# Revit family: 8_天吊埋込タイプ 厨房用 単相100V_3相200V-60
name_source: partatom
category: 機械設備
units: mm (PartAtom-declared; Revit-internal decimal feet)

## family parameters
OmniClass タイトル = Axial Fans
OmniClass 番号 = 23.75.35.17.24
パーツ タイプ = 割り込み
ロード時にボイドで切り取り = いいえ
丸型コネクタ寸法 = 直径を使用
作業面ベース = いいえ
共有 = いいえ
常に垂直 = はい
部屋計算ポイント = はい

## types (6) — shared parameters
Clearance Left = 600
IfcExportAs = IfcFanType
IfcExportType = CENTRIFUGALFORWARDCURVED
M = 85  [stored 0.278871 ft]
MID静圧 = 0.0 Pa
MID風量 = 0.0 m³/h
MIN静圧 = 0.0 Pa
MIN風量 = 0.0 m³/h
OmniClassCode = 23-33 31 19 13 15
URL = https://www.mitsubishielectric.co.jp
Uniclass2015Code = Pr_65_67_29_12
Uniclass2015Title = Centrifugal fans
Uniclass2015Version = Systems v1.9
サービススペース = はい
ドレン管径 = 18 mm
ファンの種類 = 多翼形
仕様書バージョン = Version1.0
企業コード = 108420
分類コード = 50052502100020
周波数 = 60 Hz
呼称 = 消音ボックス付送風機
極 = 4
法定耐用年数 = 15
盤工事区分 = 電気工事
積算_科目 = 2 換気設備
製品リリース年月 = 2019年6月20日
製品出荷対象 = 国内
製造元 = 三菱電機株式会社
設置方法 = 天吊
説明 = ストレートシロッコファン厨房用
負荷分類 = 3_ファン類
運転質量 = 0.00 kg
zero-valued in all types: Clearance Back, Clearance Bottom, Clearance Front, Clearance Right, Clearance Top

## per-type parameters (varying)
| type | Depth | Height | MAX静圧 | MAX風量 | Width | ダクト径 | 価格 | 天吊金具ピッチ奥行 | 天吊金具ピッチ幅 | 形名 | 本体マテリアル | 極数 | 消費電力 | 番手 | 相 | 製品質量 | 質量 | 電動機出力 | 電圧 | 騒音レベル(dB(A)) | 騒音レベル(dB(A))_側面 | 騒音レベル(dB(A))_吐出 | 騒音レベル(dB(A))_吸込 |
| BFS-50SXA | 399  [stored 1.30906 ft] | 258.4  [stored 0.847769 ft] | 207.0 Pa | 500.0 m³/h | 325  [stored 1.06627 ft] | 200 mm | 141000 $ | 362  [stored 1.18766 ft] | 401  [stored 1.31562 ft] | BFS-SXA : BFS-50SXA | SUS304 | 2 | 100 W | #1 1/4 | 1 | 12.00 kg | 14.40 kg | 55 W | 100 V | 51.5 | 31.5 | 51.5 | 48 |
| BFS-80SXA | 472 | 308.4  [stored 1.01181 ft] | 212.0 Pa | 800.0 m³/h | 343  [stored 1.12533 ft] | 200 mm | 158000 $ | 434  [stored 1.42388 ft] | 419 | BFS-SXA : BFS-80SXA | 溶融亜鉛めっき鋼板 | 2 | 200 W | #1 1/4 | 1 | 14.50 kg | 17.40 kg | 110 W | 100 V | 56 | 34.5 | 56 | 50 |
| BFS-100SXA | 490  [stored 1.60761 ft] | 308.4  [stored 1.01181 ft] | 290.0 Pa | 1000.0 m³/h | 393  [stored 1.28937 ft] | 200 mm | 173000 $ | 452  [stored 1.48294 ft] | 469 | BFS-SXA : BFS-100SXA | 溶融亜鉛めっき鋼板 | 2 | 300 W | #1 1/2 | 1 | 18.00 kg | 21.60 kg | 230 W | 100 V | 60 | 38 | 60 | 55 |
| BFS-150SXA | 542  [stored 1.77822 ft] | 353.4  [stored 1.15945 ft] | 335.0 Pa | 1500.0 m³/h | 376  [stored 1.2336 ft] | 250 mm | 197000 $ | 504  [stored 1.65354 ft] | 452  [stored 1.48294 ft] | BFS-SXA : BFS-150SXA | 溶融亜鉛めっき鋼板 | 2 | 520 W | #1 1/2 | 1 | 23.00 kg | 27.60 kg | 330 W | 100 V | 66.5 | 41.5 | 66.5 | 61.5 |
| BFS-150TXA | 542  [stored 1.77822 ft] | 353.4  [stored 1.15945 ft] | 365.0 Pa | 1500.0 m³/h | 376  [stored 1.2336 ft] | 250 mm | 197000 $ | 504  [stored 1.65354 ft] | 452  [stored 1.48294 ft] | BFS-TXA : BFS-150TXA | 溶融亜鉛めっき鋼板 | 3 | 480 W | #1 1/2 | 3 | 23.00 kg | 27.60 kg | 440 W | 200 V | 66.5 | 40 | 66.5 | 62 |
| BFS-210TXA | 572 | 353.4  [stored 1.15945 ft] | 383.0 Pa | 2100.0 m³/h | 426  [stored 1.39764 ft] | 300 mm | 278000 $ | 534  [stored 1.75197 ft] | 502  [stored 1.64698 ft] | BFS-TXA : BFS-210TXA | 溶融亜鉛めっき鋼板 | 3 | 700 W | #1 1/2 | 3 | 24.50 kg | 29.40 kg | 530 W | 200 V | 69.5 | 44 | 69.5 | 66 |

note: column(s) folded — value = type name in every type: モデル

note: [stored X ft] marks values corroborated as IEEE doubles in the binary element streams (Revit-internal decimal feet)
